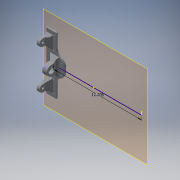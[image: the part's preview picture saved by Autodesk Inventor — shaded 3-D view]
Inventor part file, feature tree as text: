
AUTODESK INVENTOR PART (.ipt)
format: ipt  version: 2016 (Build 200138000, 138)  size: 307,200 bytes
history: native  units: in
note: dims shown in document units (in); Inventor stores cm internally (conversion verified against a paired STEP export)
features: reference x12, sketch x11, extrude x10, projected_geometry x10, chamfer x5, plane x2, fillet x2
ambient origin geometry x8: Origin, YZ Plane, XZ Plane, XY Plane, X Axis, Y Axis, Z Axis, Center Point
bodies: Solid1 (feature_tree)
feature tree (52):
  plane  "Work Plane1"
  extrude  "Extrusion1"  Depth=1.0in
  fillet  "Fillet1"  Radius=12.2047in
  sketch  "Sketch2"  dims[d4=0.0in d5=0.0in d6=0.4in d7=0.0in]
  plane  "Work Plane2"
  extrude  "Extrusion2"  Depth=0.4in TaperAngle=0.0deg
  extrude  "Extrusion3"  Depth=0.3937in
  chamfer  "Chamfer1"  Distance=0.2in
  extrude  "Extrusion4"  Depth=1.0in TaperAngle=45.0deg
  fillet  "Fillet2"  Radius=1.8625in
  chamfer  "Chamfer2"  Distance=1.0in
  extrude  "Extrusion5"  Depth=0.5625in TaperAngle=45.0deg
  extrude  "Extrusion6"  Depth=1.0in TaperAngle=0.0deg
  chamfer  "Chamfer3"  Distance=0.0787in
  chamfer  "Chamfer4"  Distance=1.4838in
  chamfer  "Chamfer5"  Distance=0.1in
  extrude  "Extrusion7"  [1 undecoded]
  extrude  "Extrusion8"  [1 undecoded]
  extrude  "Extrusion9"  [1 undecoded]
  extrude  "Extrusion10"  [1 undecoded]
  sketch  "Sketch1"  dims[d0=0.2in d1=0.0in d2=1.0in d3=12.2047in]
  reference  "Reference1"
  reference  "Reference2"
  reference  "Reference3"
  reference  "Reference4"
  reference  "Reference5"
  reference  "Reference6"
  reference  "Reference7"
  reference  "Reference8"
  sketch  "Sketch3"  dims[d8=0.5625in d9=0.125in d10=45.0deg d11=0.3937in d12=0.2in d13=0.0in]
  reference  "Reference9"
  reference  "Reference10"
  reference  "Reference11"
  sketch  "Sketch4"  dims[d14=0.375in d15=0.5625in d16=0.125in d17=45.0deg d18=1.8625in d19=0.0in d20=1.0in d21=0.0in]
  projected_geometry  "Projected Loop1"
  projected_geometry  "Projected Loop2"
  sketch  "Sketch5"  dims[d22=0.5625in d23=0.125in d24=45.0deg d25=0.5625in d26=0.125in d27=45.0deg]
  projected_geometry  "Projected Loop3"
  sketch  "Sketch6"  dims[d28=0.25in d29=0.125in d30=45.0deg d31=1.0in d32=0.0in d33=0.0787in d34=0.0in d35=1.4838in d36=0.0in d37=0.1in d38=0.0in]
  projected_geometry  "Projected Loop4"
  projected_geometry  "Projected Loop5"
  projected_geometry  "Projected Loop6"
  projected_geometry  "Projected Loop7"
  sketch  "Sketch7"
  projected_geometry  "Projected Loop8"
  sketch  "Sketch8"
  reference  "Reference12"
  sketch  "Sketch9"
  projected_geometry  "Projected Loop9"
  sketch  "Sketch10"
  sketch  "Sketch11"
  projected_geometry  "Projected Loop10"
note: 4 required parameter values undecoded (feature->parameter linkage not recoverable at this tier; creation-order binding heuristic only, values carry confidence <= 0.55)
